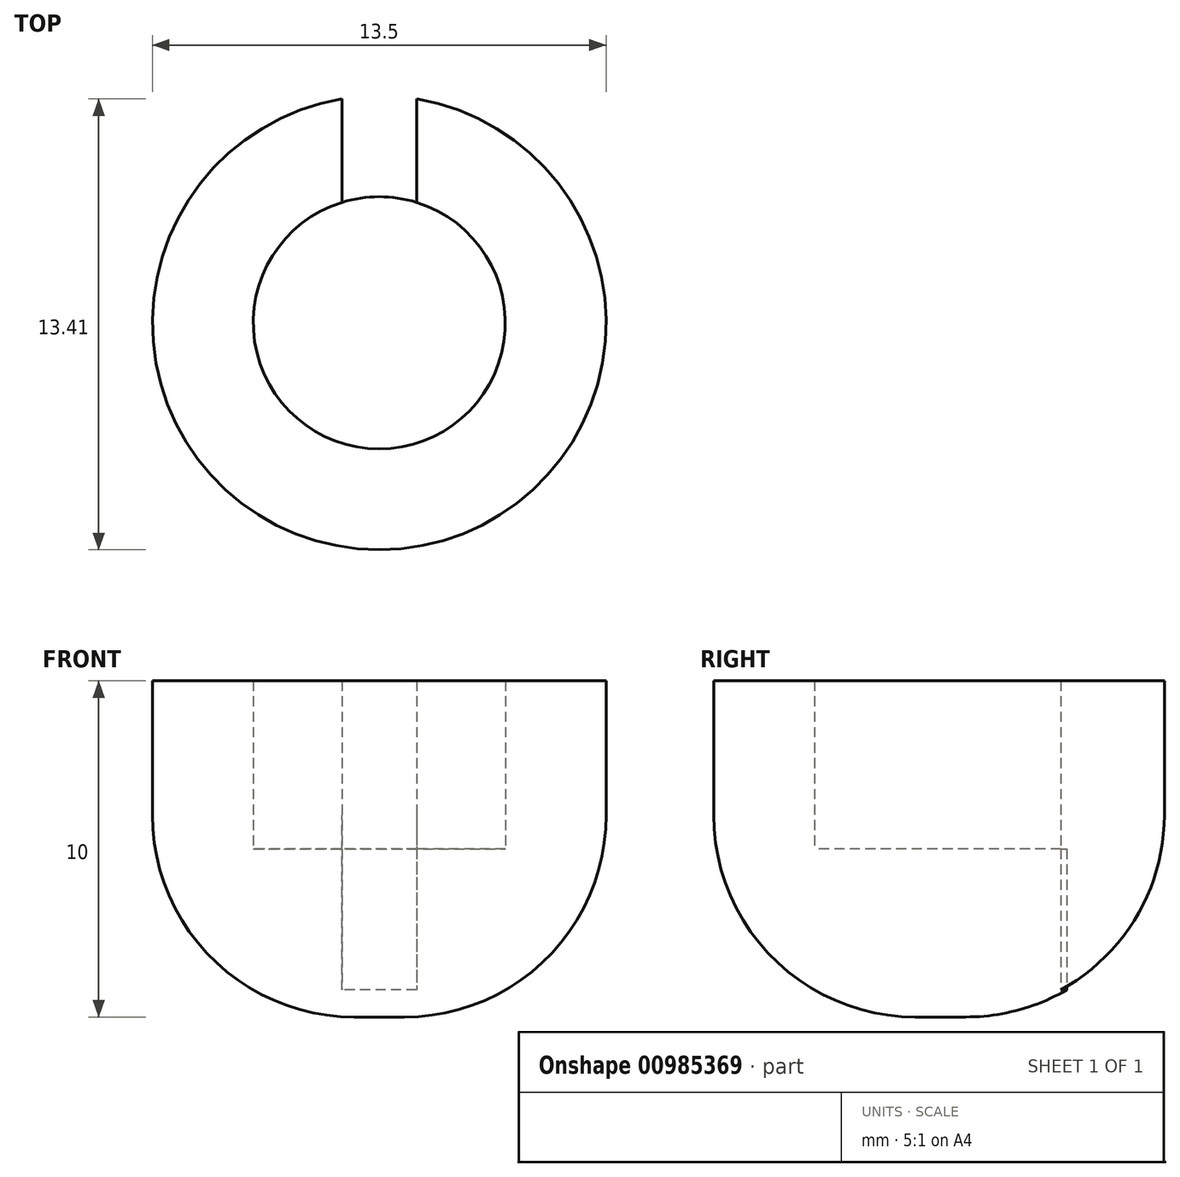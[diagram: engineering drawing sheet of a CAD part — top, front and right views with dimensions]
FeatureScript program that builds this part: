
annotation { "Feature Type Name" : "Feature", "Feature Type Description" : "" }
export const myFeature = defineFeature(function(context is Context, id is Id, definition is map)
    precondition{}
    {
        {
            var Q0;
            Q0=qCreatedBy(makeId("Top.planeOp"),FACE);
            var sketch = newSketch(context, id + "F0", { "sketchPlane" : qUnion([Q0])});
            skCircle(sketch, "E0", {"center": v(0, 0) * mm, "radius": 3.75 * mm});
            skCircle(sketch, "E1", {"center": v(0, 0) * mm, "radius": 6.75 * mm});
            skLineSegment(sketch, "E2.bottom", {"start": v(1.1, 0.75) * mm, "end": v(-1.1, 0.75) * mm});
            skLineSegment(sketch, "E2.top", {"start": v(1.1, 6.75) * mm, "end": v(-1.1, 6.75) * mm});
            skLineSegment(sketch, "E2.left", {"start": v(1.1, 0.75) * mm, "end": v(1.1, 6.75) * mm});
            skLineSegment(sketch, "E2.right", {"start": v(-1.1, 0.75) * mm, "end": v(-1.1, 6.75) * mm});
            skPoint(sketch, "E2.middle", {"position": v(0, 3.75) * mm});
            skSolve(sketch);
        }
        {
            var Q0;
            {var subQ0=sQuery(id+"F0.wireOp",EDGE,"E2.left");var subQ1=sQuery(id+"F0.wireOp",EDGE,"E0");var subQ2=makeQuery(id+"F0.imprint","INTERSECT",VERTEX,{"derivedFrom":[subQ1,subQ0]});Q0=makeQuery(id+"F0.imprint","IMPRINT",FACE,{"disambiguationData":[TD([[makeQuery(id+"F0.imprint","IMPRINT",EDGE,{"disambiguationData":[TD([[subQ2,1.0]])],"derivedFrom":subQ1}),-1.0]])]});}
            extrude(context, id + "F1", {"entities" : qUnion([Q0]), "depth" : 10 * mm, "offsetDistance" : 25 * mm});
        }
        {
            var Q0;
            {var subQ5=sQuery(id+"F0.wireOp",EDGE,"E2.bottom");Q0=makeQuery(id+"F0.imprint","IMPRINT",FACE,{"disambiguationData":[TD([[makeQuery(id+"F0.imprint","IMPRINT",EDGE,{"derivedFrom":subQ5}),1.0]])]});}
            var Q1;
            {var subQ5=sQuery(id+"F0.wireOp",EDGE,"E2.bottom");Q1=makeQuery(id+"F0.imprint","IMPRINT",FACE,{"disambiguationData":[TD([[makeQuery(id+"F0.imprint","IMPRINT",EDGE,{"derivedFrom":subQ5}),-1.0]])]});}
            extrude(context, id + "F2", {"entities" : qUnion([Q0, Q1]), "operationType" : NewBodyOperationType.ADD, "depth" : 5 * mm, "offsetDistance" : 25 * mm});
        }
        {
            var Q0;
            Q0=makeQuery(id+"F1.opExtrude","CAP_EDGE",EDGE,{"disambiguationData":[OSD([sQuery(id+"F0.wireOp",EDGE,"E1")])],"isStart":true});
            fillet(context, id + "F3", {"entities" : qUnion([Q0]), "radius" : 6 * mm, "tangentPropagation" : true, "allowEdgeOverflow" : false});
        }
    });
